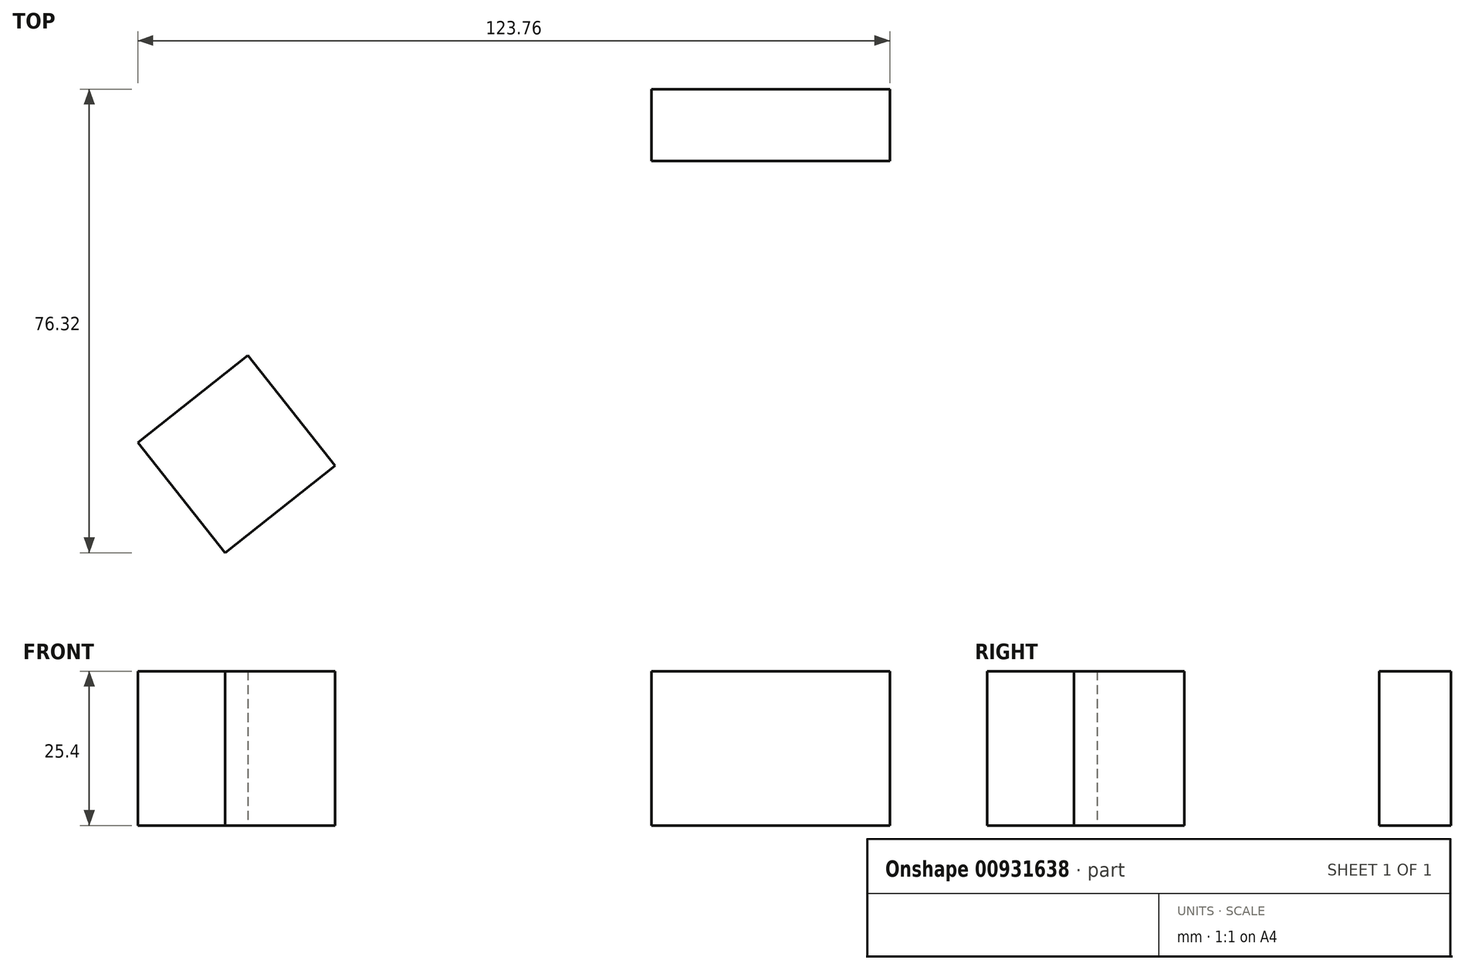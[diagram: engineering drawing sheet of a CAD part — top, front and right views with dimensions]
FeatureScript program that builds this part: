
annotation { "Feature Type Name" : "Feature", "Feature Type Description" : "" }
export const myFeature = defineFeature(function(context is Context, id is Id, definition is map)
    precondition{}
    {
        {
            var Q0;
            Q0=qCreatedBy(makeId("Top.planeOp"),FACE);
            var sketch = newSketch(context, id + "F0", { "sketchPlane" : qUnion([Q0])});
            skEllipse(sketch, "E0", {"center": v(-47.33, 36.68) * mm, "majorRadius": 27.74 * mm, "minorRadius": 12.6 * mm, "majorAxis": v(0.2, -0.98)});
            skLineSegment(sketch, "E1.bottom", {"start": v(5.38, 27.62) * mm, "end": v(44.6, 27.62) * mm});
            skLineSegment(sketch, "E1.top", {"start": v(5.38, 15.81) * mm, "end": v(44.6, 15.81) * mm});
            skLineSegment(sketch, "E1.left", {"start": v(5.38, 27.62) * mm, "end": v(5.38, 15.81) * mm});
            skLineSegment(sketch, "E1.right", {"start": v(44.6, 27.62) * mm, "end": v(44.6, 15.81) * mm});
            skFitSpline(sketch, "E2", {"points": [v(-32.36, -27.62) * mm, v(17.82, -16.87) * mm, v(35.74, -33.52) * mm, v(53.45, -14.13) * mm, v(59.98, -23.2) * mm], "startDerivative": vector(166.4, 77.83) * mm, "endDerivative": vector(32.98, -94.16) * mm});
            skCircle(sketch, "E3.cCircle", {"center": v(-62.93, -32.47) * mm, "radius": 11.56 * mm, "construction": true});
            skLineSegment(sketch, "E3.0", {"start": v(-61.04, -16.23) * mm, "end": v(-46.7, -34.37) * mm});
            skLineSegment(sketch, "E3.1", {"start": v(-46.7, -34.37) * mm, "end": v(-64.83, -48.7) * mm});
            skLineSegment(sketch, "E3.2", {"start": v(-64.83, -48.7) * mm, "end": v(-79.17, -30.57) * mm});
            skLineSegment(sketch, "E3.3", {"start": v(-79.17, -30.57) * mm, "end": v(-61.04, -16.23) * mm});
            skPoint(sketch, "E3.0.midPoint", {"position": v(-53.87, -25.3) * mm});
            skSolve(sketch);
        }
        {
            var Q0;
            Q0=makeQuery(id+"F0.imprint","IMPRINT",FACE,{"disambiguationData":[TD([[makeQuery(id+"F0.imprint","IMPRINT",EDGE,{"derivedFrom":sQuery(id+"F0.wireOp",EDGE,"E3.0")}),-1.0]])]});
            var Q1;
            Q1=makeQuery(id+"F0.imprint","IMPRINT",FACE,{"disambiguationData":[TD([[makeQuery(id+"F0.imprint","IMPRINT",EDGE,{"derivedFrom":sQuery(id+"F0.wireOp",EDGE,"E1.bottom")}),-1.0]])]});
            extrude(context, id + "F1", {"entities" : qUnion([Q0, Q1]), "depth" : 25.4 * mm, "offsetDistance" : 25.4 * mm});
        }
    });
